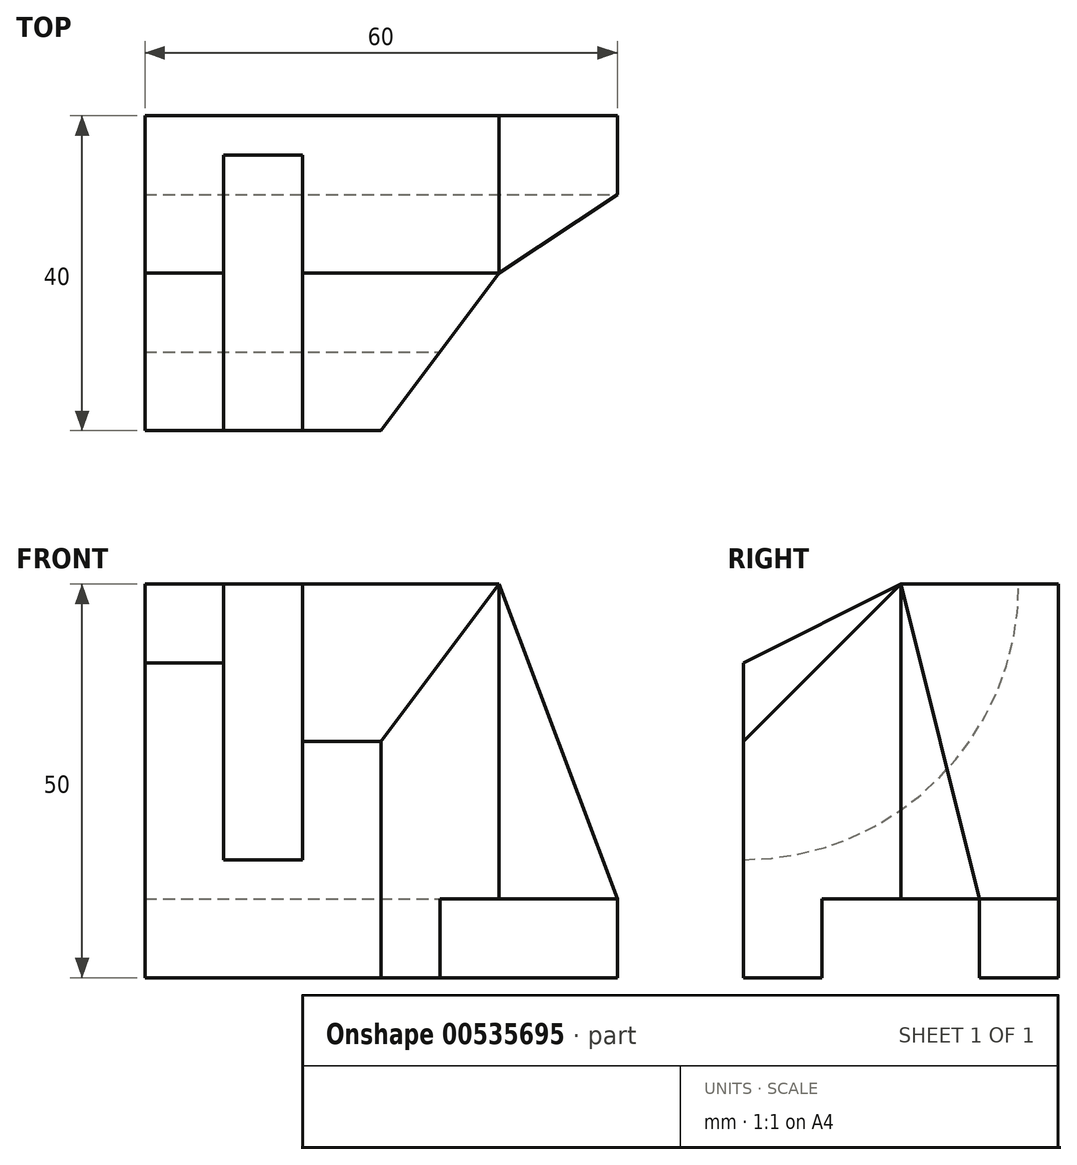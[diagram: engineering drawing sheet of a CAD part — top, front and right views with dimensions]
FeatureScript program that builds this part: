
annotation { "Feature Type Name" : "Feature", "Feature Type Description" : "" }
export const myFeature = defineFeature(function(context is Context, id is Id, definition is map)
    precondition{}
    {
        {
            var Q0;
            Q0=qCreatedBy(makeId("Top.planeOp"),FACE);
            var sketch = newSketch(context, id + "F0", { "sketchPlane" : qUnion([Q0])});
            skLineSegment(sketch, "E0.bottom", {"start": v(0, 0) * mm, "end": v(60, 0) * mm});
            skLineSegment(sketch, "E0.top", {"start": v(0, 40) * mm, "end": v(60, 40) * mm});
            skLineSegment(sketch, "E0.left", {"start": v(0, 0) * mm, "end": v(0, 40) * mm});
            skLineSegment(sketch, "E0.right", {"start": v(60, 0) * mm, "end": v(60, 40) * mm});
            skSolve(sketch);
        }
        {
            var Q0;
            Q0 = qSketchRegion(id + "F0", true);
            extrude(context, id + "F1", {"entities" : qUnion([Q0]), "depth" : 50 * mm, "offsetDistance" : 25 * mm});
        }
        {
            var Q0;
            Q0=makeQuery(id+"F1.opExtrude","CAP_FACE",FACE,{"disambiguationData":[OSD([sQuery(id+"F0.wireOp",EDGE,"E0.bottom"),sQuery(id+"F0.wireOp",EDGE,"E0.top"),sQuery(id+"F0.wireOp",EDGE,"E0.left"),sQuery(id+"F0.wireOp",EDGE,"E0.right")])],"isStart":false});
            var sketch = newSketch(context, id + "F2", { "sketchPlane" : qUnion([Q0])});
            skLineSegment(sketch, "E1.bottom", {"start": v(10, 0) * mm, "end": v(20, 0) * mm});
            skLineSegment(sketch, "E1.top", {"start": v(10, 35) * mm, "end": v(20, 35) * mm});
            skLineSegment(sketch, "E1.left", {"start": v(10, 0) * mm, "end": v(10, 35) * mm});
            skLineSegment(sketch, "E1.right", {"start": v(20, 0) * mm, "end": v(20, 35) * mm});
            skSolve(sketch);
        }
        {
            var Q0;
            Q0 = qSketchRegion(id + "F2", true);
            extrude(context, id + "F3", {"entities" : qUnion([Q0]), "operationType" : NewBodyOperationType.REMOVE, "oppositeDirection" : true, "depth" : 35 * mm, "offsetDistance" : 25 * mm});
        }
        {
            var Q0;
            Q0=makeQuery(id+"F3.boolean.opBoolean","COPY",EDGE,{"derivedFrom":makeQuery(id+"F3.opExtrude","CAP_EDGE",EDGE,{"disambiguationData":[OSD([sQuery(id+"F2.wireOp",EDGE,"E1.top")])],"isStart":false})});
            fillet(context, id + "F4", {"entities" : qUnion([Q0]), "radius" : 35 * mm, "tangentPropagation" : true, "allowEdgeOverflow" : false});
        }
        {
            var Q0;
            Q0=makeQuery(id+"F1.opExtrude","SWEPT_FACE",FACE,{"disambiguationData":[OSD([sQuery(id+"F0.wireOp",EDGE,"E0.left")])]});
            var sketch = newSketch(context, id + "F5", { "sketchPlane" : qUnion([Q0])});
            skLineSegment(sketch, "E2", {"start": v(-20, 50) * mm, "end": v(0, 40) * mm});
            skLineSegment(sketch, "E3", {"start": v(0, 40) * mm, "end": v(0, 50) * mm});
            skLineSegment(sketch, "E4", {"start": v(0, 50) * mm, "end": v(-20, 50) * mm});
            skSolve(sketch);
        }
        {
            var Q0;
            Q0 = qSketchRegion(id + "F5", true);
            extrude(context, id + "F6", {"entities" : qUnion([Q0]), "operationType" : NewBodyOperationType.REMOVE, "endBound" : BoundingType.UP_TO_NEXT, "oppositeDirection" : true, "depth" : 25 * mm, "offsetDistance" : 25 * mm});
        }
        {
            var Q0;
            Q0=makeQuery(id+"F1.opExtrude","CAP_FACE",FACE,{"disambiguationData":[OSD([sQuery(id+"F0.wireOp",EDGE,"E0.bottom"),sQuery(id+"F0.wireOp",EDGE,"E0.top"),sQuery(id+"F0.wireOp",EDGE,"E0.left"),sQuery(id+"F0.wireOp",EDGE,"E0.right")])],"isStart":false});
            var sketch = newSketch(context, id + "F7", { "sketchPlane" : qUnion([Q0])});
            skLineSegment(sketch, "E5", {"start": v(30, 0) * mm, "end": v(45, 20) * mm});
            skLineSegment(sketch, "E6", {"start": v(45, 20) * mm, "end": v(60, 30) * mm});
            skLineSegment(sketch, "E7", {"start": v(60, 30) * mm, "end": v(60, 0) * mm});
            skLineSegment(sketch, "E8", {"start": v(60, 0) * mm, "end": v(30, 0) * mm});
            skSolve(sketch);
        }
        {
            var Q0;
            Q0 = qSketchRegion(id + "F7", true);
            extrude(context, id + "F8", {"entities" : qUnion([Q0]), "operationType" : NewBodyOperationType.REMOVE, "endBound" : BoundingType.THROUGH_ALL, "oppositeDirection" : true, "depth" : 25 * mm, "offsetDistance" : 25 * mm});
        }
        {
            var Q0;
            Q0=makeQuery(id+"F1.opExtrude","SWEPT_FACE",FACE,{"disambiguationData":[OSD([sQuery(id+"F0.wireOp",EDGE,"E0.top")])]});
            var sketch = newSketch(context, id + "F9", { "sketchPlane" : qUnion([Q0])});
            skLineSegment(sketch, "E9", {"start": v(-60, 50) * mm, "end": v(-45, 50) * mm});
            skLineSegment(sketch, "E10", {"start": v(-45, 50) * mm, "end": v(-60, 10) * mm});
            skLineSegment(sketch, "E11", {"start": v(-60, 10) * mm, "end": v(-60, 50) * mm});
            skSolve(sketch);
        }
        {
            var Q0;
            Q0 = qSketchRegion(id + "F9", true);
            extrude(context, id + "F10", {"entities" : qUnion([Q0]), "operationType" : NewBodyOperationType.REMOVE, "endBound" : BoundingType.THROUGH_ALL, "oppositeDirection" : true, "depth" : 25 * mm, "offsetDistance" : 25 * mm});
        }
        {
            var Q0;
            Q0=qCreatedBy(makeId("Right.planeOp"),FACE);
            cPlane(context, id + "F11", {"entities" : qUnion([Q0]), "cplaneType" : CPlaneType.OFFSET, "offset" : 60 * mm, "width" : 150 * mm, "height" : 150 * mm});
        }
        {
            var Q0;
            Q0=qCreatedBy(id+"F11.planeOp",FACE);
            var sketch = newSketch(context, id + "F12", { "sketchPlane" : qUnion([Q0])});
            skLineSegment(sketch, "E12.bottom", {"start": v(10, 0) * mm, "end": v(30, 0) * mm});
            skLineSegment(sketch, "E12.top", {"start": v(10, 10) * mm, "end": v(30, 10) * mm});
            skLineSegment(sketch, "E12.left", {"start": v(10, 0) * mm, "end": v(10, 10) * mm});
            skLineSegment(sketch, "E12.right", {"start": v(30, 0) * mm, "end": v(30, 10) * mm});
            skSolve(sketch);
        }
        {
            var Q0;
            Q0 = qSketchRegion(id + "F12", true);
            extrude(context, id + "F13", {"entities" : qUnion([Q0]), "operationType" : NewBodyOperationType.REMOVE, "endBound" : BoundingType.THROUGH_ALL, "oppositeDirection" : true, "depth" : 25 * mm, "offsetDistance" : 25 * mm});
        }
        {
            var Q0;
            Q0=makeQuery(id+"F1.opExtrude","SWEPT_FACE",FACE,{"disambiguationData":[OSD([sQuery(id+"F0.wireOp",EDGE,"E0.bottom")])]});
            var sketch = newSketch(context, id + "F14", { "sketchPlane" : qUnion([Q0])});
            skPoint(sketch, "E13", {"position": v(30, 30) * mm});
            skSolve(sketch);
        }
        {
            var Q0;
            Q0=makeQuery(id+"F8.boolean.opBoolean","COPY",VERTEX,{"derivedFrom":makeQuery(id+"F8.opExtrude","CAP_VERTEX",VERTEX,{"disambiguationData":[OSD([sQuery(id+"F7.wireOp",EDGE,"E5"),sQuery(id+"F7.wireOp",EDGE,"E6")])],"isStart":true})});
            var Q1;
            Q1=makeQuery(id+"F6.boolean.opBoolean","COPY",VERTEX,{"derivedFrom":makeQuery(id+"F6.opExtrude","CAP_VERTEX",VERTEX,{"disambiguationData":[OSD([sQuery(id+"F0.wireOp",EDGE,"E0.left"),sQuery(id+"F2.wireOp",EDGE,"E1.left"),sQuery(id+"F5.wireOp",EDGE,"E2"),sQuery(id+"F5.wireOp",EDGE,"E4")])],"isStart":false})});
            var Q2;
            Q2=sQuery(id+"F14.wireOp",VERTEX,"E13");
            cPlane(context, id + "F15", {"entities" : qUnion([Q0, Q1, Q2]), "cplaneType" : CPlaneType.THREE_POINT, "offset" : 25 * mm, "width" : 150 * mm, "height" : 150 * mm});
        }
        {
            var Q0;
            Q0=makeQuery(id+"F1.opExtrude","CAP_FACE",FACE,{"disambiguationData":[OSD([sQuery(id+"F0.wireOp",EDGE,"E0.bottom"),sQuery(id+"F0.wireOp",EDGE,"E0.top"),sQuery(id+"F0.wireOp",EDGE,"E0.left"),sQuery(id+"F0.wireOp",EDGE,"E0.right")])],"isStart":false});
            var sketch = newSketch(context, id + "F16", { "sketchPlane" : qUnion([Q0])});
            skLineSegment(sketch, "E14", {"start": v(45, 20) * mm, "end": v(20, 20) * mm});
            skLineSegment(sketch, "E15", {"start": v(20, 20) * mm, "end": v(20, 0) * mm});
            skLineSegment(sketch, "E16", {"start": v(20, 0) * mm, "end": v(30, 0) * mm});
            skLineSegment(sketch, "E17", {"start": v(30, 0) * mm, "end": v(45, 20) * mm});
            skSolve(sketch);
        }
        {
            var Q0;
            Q0 = qSketchRegion(id + "F16", true);
            var Q1;
            Q1=qCreatedBy(id+"F15.planeOp",FACE);
            extrude(context, id + "F17", {"entities" : qUnion([Q0]), "operationType" : NewBodyOperationType.REMOVE, "endBound" : BoundingType.UP_TO_SURFACE, "oppositeDirection" : true, "depth" : 25 * mm, "endBoundEntityFace" : qUnion([Q1]), "offsetDistance" : 25 * mm});
        }
    });
